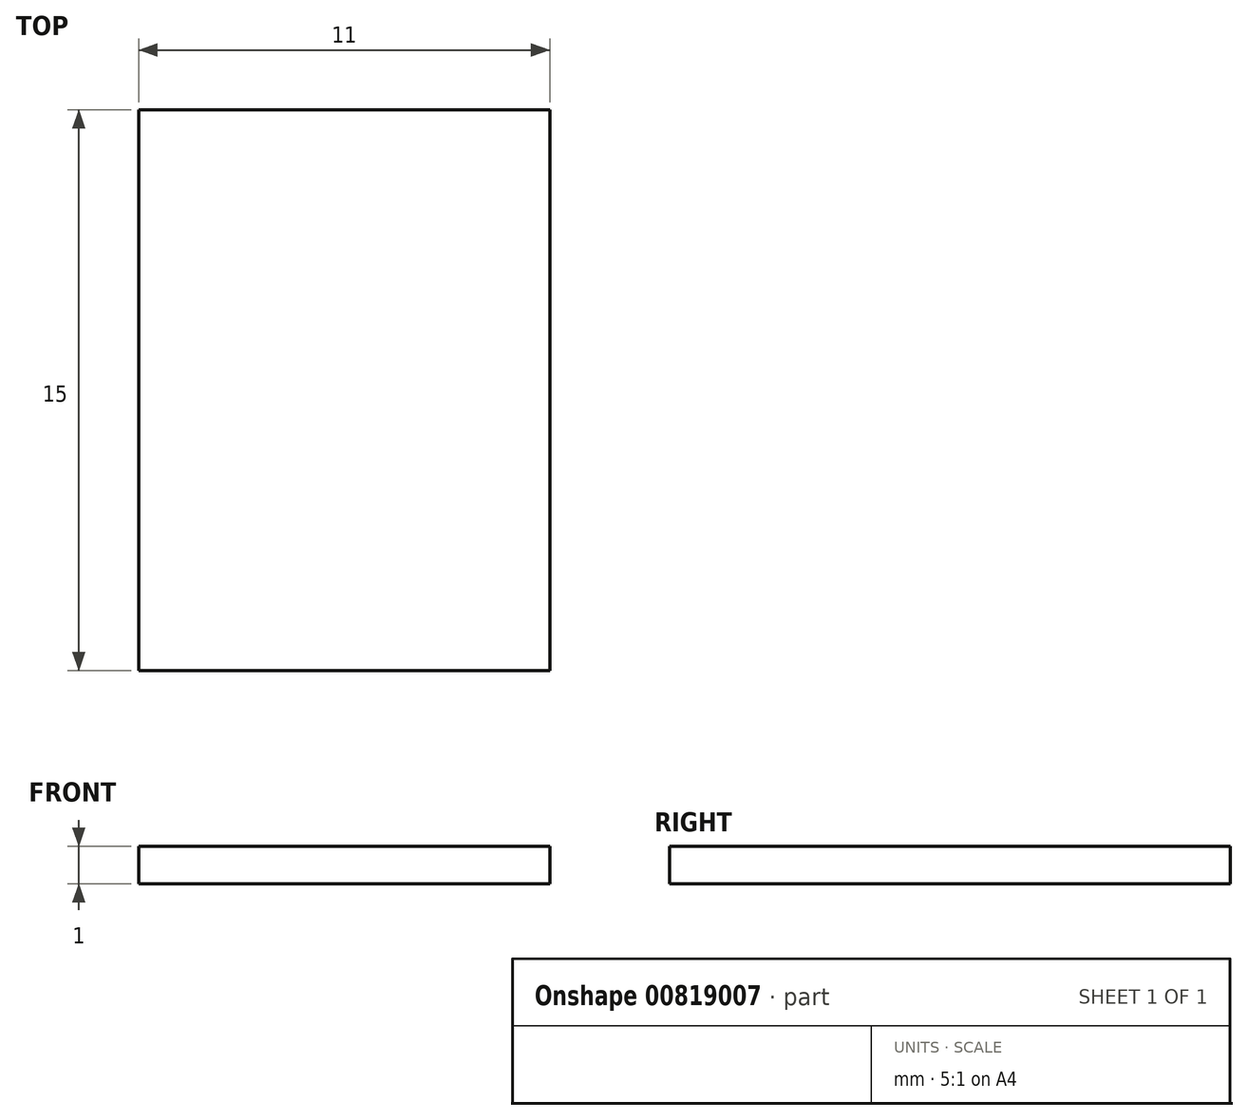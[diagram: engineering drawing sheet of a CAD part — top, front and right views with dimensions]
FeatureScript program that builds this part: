
annotation { "Feature Type Name" : "Feature", "Feature Type Description" : "" }
export const myFeature = defineFeature(function(context is Context, id is Id, definition is map)
    precondition{}
    {
        {
            var Q0;
            Q0=qCreatedBy(makeId("Top.planeOp"),FACE);
            var sketch = newSketch(context, id + "F0", { "sketchPlane" : qUnion([Q0])});
            skLineSegment(sketch, "E0.bottom", {"start": v(5.5, -7.5) * mm, "end": v(-5.5, -7.5) * mm});
            skLineSegment(sketch, "E0.top", {"start": v(5.5, 7.5) * mm, "end": v(-5.5, 7.5) * mm});
            skLineSegment(sketch, "E0.left", {"start": v(5.5, -7.5) * mm, "end": v(5.5, 7.5) * mm});
            skLineSegment(sketch, "E0.right", {"start": v(-5.5, -7.5) * mm, "end": v(-5.5, 7.5) * mm});
            skPoint(sketch, "E0.middle", {"position": v(0, 0) * mm});
            skSolve(sketch);
        }
        {
            var Q0;
            Q0 = qSketchRegion(id + "F0", true);
            extrude(context, id + "F1", {"entities" : qUnion([Q0]), "depth" : 1 * mm, "offsetDistance" : 25 * mm});
        }
    });
